# Revit family: Gira_536727
name_source: partatom
category: Electrical Fixtures
revit_build: Autodesk Revit 2017 (Build: 20160225_1515(x64)
units: mm (PartAtom-declared; Revit-internal decimal feet)

## family parameters
Cut with Voids When Loaded = No
Host = Face
Maintain Annotation Orientation = No
Part Type = Normal
Room Calculation Point = No
Round Connector Dimension = Use Diameter
Shared = No

## types (1)
- S3000 blind timer + timer BT System 55 p.white m
    Application = Control of electrical users
    Available = No
    BIM (1) = https://media.stage.bim.site und Tasten.rfa?public/gira/36a6b08/Sys55_Abdeckung_Schalten und Tasten.rfa
    Category = Intelligent control element
    Data sheet (1) = https://katalog.gira.de
    Default Elevation = 1219 mm
    Description = S3000 blind tim. tim.BT Sys55 PWm,System 3000 blind timer and timer BT,,pure white matt,Features:,- Manual and time-controlled operation of e.g. blinds, shutters, awnings, lighting or fans.,- Operation and programming with mobile end device (smartphone or tablet) via Bluetooth using the Gira Bluetooth app.,- Operation on System 3000 switching, dimming or blind insert or auxiliary insert 3-wire.,Functions on the top unit:,- Operation of hangings and lighting.,- The blocking function blocks operation of the auxiliary unit and deactivates automatic mode.,- Activate deactivate automatic mode.,- The runtime and an individual intermediate position can be saved using the System 3000 blind controller insert.,- Switch-on brightness of lighting can be saved using System 3000 dimming insert or DALI Power control unit.,- Adjustbable night mode. Status LED and function LED are not lit up continuously.,Functions with the Gira Bluetooth app:,- Operation of hangings and lighting with status feedback.,- Display the current hanging position or dimmer setting.,- Programming of up to 40 individual switching times.,- Blind or slat positions or switching and dimming values can be stored for each switching time.,- Switching times can be copied to other devices.,- Switching at sunrise or sunset (astro function).,- Astro time can be optimised by determining the location.,- Astro time shift adjustable.,- Random function.,- Automatic date and time refresh when connecting smartphones or tablets.,- Password protection possible for time programs and configuration (as of app version 2).,- Save a hanging position, hanging runtime, slat reversal time.,- Changeover to inverse operation possible for blind inserts.,- Maximum brightness and minimum brightness adjustable for dimming insert.,- Optional: Sun protection and twilight function are possible with System 3000 brightness and temperature sensor Bluetooth.,,Notes :,- The time is updated upon connection to the Gira Bluetooth app.
    GTIN = 4010337027539
    HAN = 536727
    HeinzeBIM = https://bimportal.heinze.de
    Manufacturer = Gira
    Manufacturer URL = https://www.gira.de
    Name = S3000 blind timer + timer BT System 55 p.white m
    Number of actuation points = 4
    Suitable for application with dimmer = No
    Suitable for application with switch = Yes
    Suitable for application with venetian shutter switch = Yes
    Transparent = No
    URL = http://katalog.gira.de
    With LED indication = No

## geometry (parser evidence)
native form markers: Blend x2, Sweep x9
no freeform markers — native parametric forms only
